# Revit family: ITK_Адаптер проходной GENERICA_категория 5E_IP20
name_source: partatom
category: Обобщенные модели
units: mm (PartAtom-declared; Revit-internal decimal feet)

## family parameters
Всегда вертикально = Да
Может служить основой для арматурных стержней = Нет
На основе рабочей плоскости = Нет
Общий = Нет
При загрузке вырезать с полостями = Нет
Размер круглого соединителя = Использовать диаметр
Тип детали = Нормальный
Точка расчета площади = Нет

## types (2) — shared parameters
ADSK_URL страницы изделия = https://generica.su
ADSK_Версия Revit = 2019
ADSK_Версия семейства = 1.0
ADSK_Группирование = I. ЩИТЫ И ПУЛЬТЫ
ADSK_Единица измерения = шт
ADSK_Завод-изготовитель = IEK
ADSK_Материал наименование = Пластик
IEK_URL = https://generica.su
KSI_CMa_Строительные материалы = 01.7.14.03
KSI_CPr_Строительные изделия = 61.1.03.04
URL = https://www.iek.ru
Высота = 24 мм
Глубина = 66 мм
Изготовитель = ITK
Ширина = 36 мм
zero-valued in all types: ADSK_Масса

## per-type parameters (varying)
| type | ADSK_Код изделия | ADSK_Наименование | IEK_Описание | IEK_Цена за единицу | Материал |
| 5E_FTP | CS80-1C5EF-G | Адаптер проходной кат. 5E FTP тип IDC-IDC (Krone) GENERICA | спользуется для удлинения имеющейся кабельной линии, объединения двух кабельных участков между собой. | 184.48 | Пластик белый |
| 5E_UTP | CS80-1C5EU-G | Адаптер проходной кат. 5E UTP тип IDC-IDC (Krone) GENERICA | Используется для удлинения имеющейся кабельной линии, объединения двух кабельных участков между собой. | 150.22 | Окраска - RAL 9005 |
